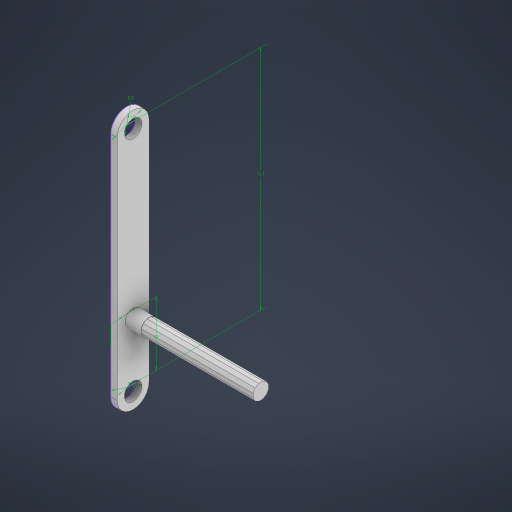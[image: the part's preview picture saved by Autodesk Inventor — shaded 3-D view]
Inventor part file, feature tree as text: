
AUTODESK INVENTOR PART (.ipt)
format: ipt  version: 2024.1 (Build 281209000, 209)  size: 509,440 bytes
history: native  units: mm
features: extrude x3, other x1, sketch x1
ambient origin geometry x8: Origin, YZ Plane, XZ Plane, XY Plane, X Axis, Y Axis, Z Axis, Center Point
bodies: Body1 (feature_tree)
feature tree (5):
  other  "솔리드1"
  sketch  "스케치1"
  extrude  "돌출1"  Depth=5.0mm
  extrude  "돌출2"  Depth=5.5mm
  extrude  "돌출3"  Depth=10.0mm
